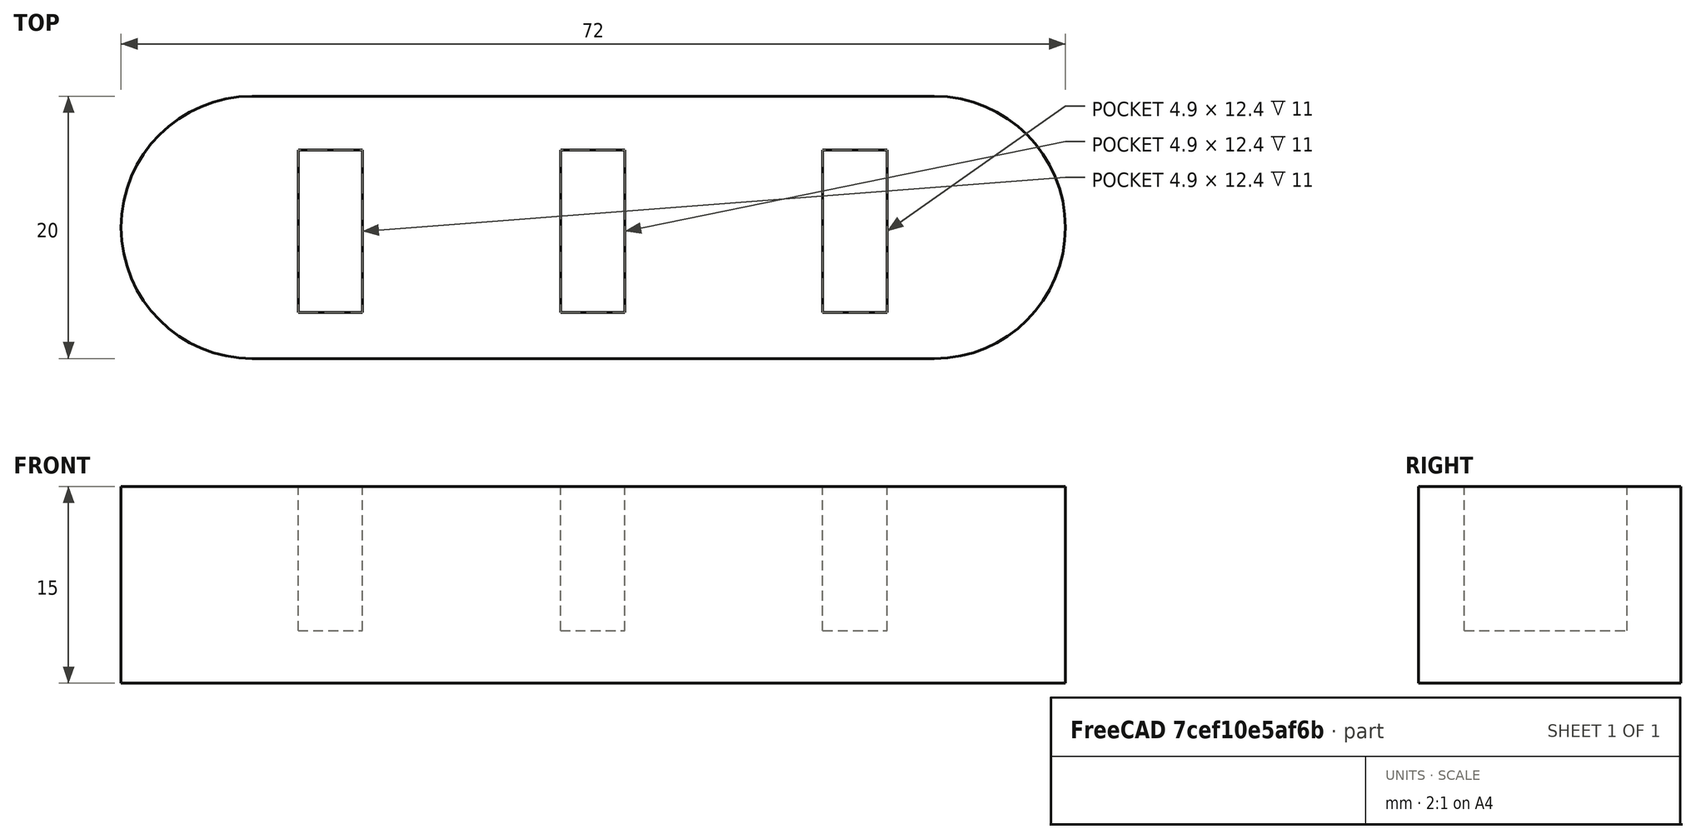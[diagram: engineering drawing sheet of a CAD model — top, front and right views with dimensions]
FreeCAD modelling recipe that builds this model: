
FCSTD DOCUMENT  (FreeCAD 0.17R13217 (Git))
Label: 07-porta-pendrive-redondeado
License: All rights reserved
LicenseURL: http://en.wikipedia.org/wiki/All_rights_reserved
objects: Part::Box×4, Part::MultiFuse×2, Part::Cylinder×2, Part::Cut×1
note: 9 computed .brp shape members not serialized (recipe doc carries the construction recipe); baked Part::Feature solids carry a one-line shape summary decoded from their .brp

FEATURE [Part::Box] Box  label="base"
  AttacherType = Attacher::AttachEngine3D
  Height = 15
  Length = 52
  Width = 20
FEATURE [Part::Box] Box001  label="slot1"
  AttacherType = Attacher::AttachEngine3D
  Height = 20
  Length = 4.9
  Placement = pos=(3.5,3.5,4) rot=(0,0,1;0rad)
  Width = 12.4
FEATURE [Part::Box] Box002  label="slot002"
  AttacherType = Attacher::AttachEngine3D
  Height = 20
  Length = 4.9
  Placement = pos=(23.5,3.5,4) rot=(0,0,1;0rad)
  Width = 12.4
FEATURE [Part::Box] Box003  label="slot003"
  AttacherType = Attacher::AttachEngine3D
  Height = 20
  Length = 4.9
  Placement = pos=(43.5,3.5,4) rot=(0,0,1;0rad)
  Width = 12.4
FEATURE [Part::MultiFuse] Fusion  label="slots"
  Refine = true
  Shapes = -> [Box001,Box003,Box002]
FEATURE [Part::Cylinder] Cylinder  label="Cilindro"
  Angle = 360
  AttacherType = Attacher::AttachEngine3D
  Height = 15
  Placement = pos=(0,10,0) rot=(0,0,1;0rad)
  Radius = 10
FEATURE [Part::Cylinder] Cylinder001  label="Cilindro001"
  Angle = 360
  AttacherType = Attacher::AttachEngine3D
  Height = 15
  Placement = pos=(52,10,0) rot=(0,0,1;0rad)
  Radius = 10
FEATURE [Part::MultiFuse] Fusion001
  Refine = true
  Shapes = -> [Box,Cylinder,Cylinder001]
FEATURE [Part::Cut] Cut
  Base = -> Fusion001
  Refine = true
  Tool = -> Fusion
